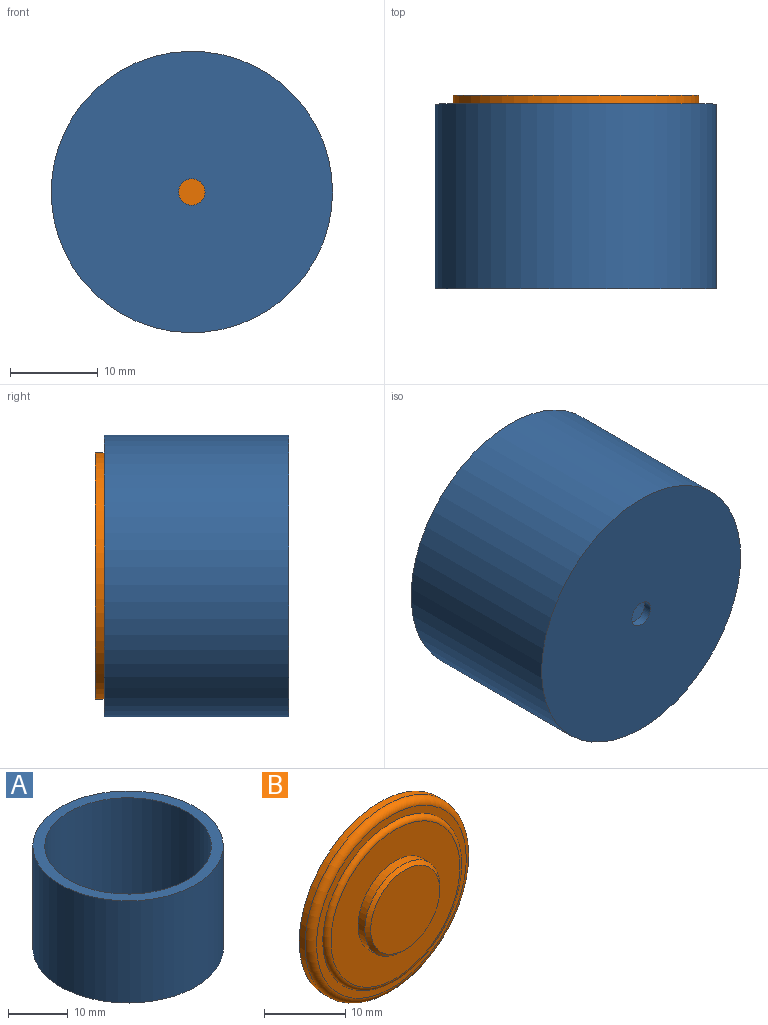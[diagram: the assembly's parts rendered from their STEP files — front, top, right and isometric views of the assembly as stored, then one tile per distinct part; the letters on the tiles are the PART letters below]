
ASSEMBLY  parts=2 mates=1
PART A: 6 faces, bbox 32x32x21 mm
  f0: cylinder r=16mm len=32mm, axis (0,0,-1), area 2111.2mm2, adj f3,f5
  f1: cylinder r=1.5mm len=3mm, axis (0,0,-1), area 9.4mm2, adj f2,f3
  f2: plane 28x28mm, normal (0,0,1), area 608.7mm2, adj f1,f4
  f3: plane 32x32mm, normal (0,0,-1), area 797.2mm2, adj f0,f1
  f4: cylinder r=14mm len=28mm, axis (0,0,-1), area 1759.3mm2, adj f2,f5
  f5: plane 32x32mm, normal (0,0,1), area 188.5mm2, adj f0,f4
PART B: 13 faces, bbox 30.3x4.4x30.3 mm
  f0: torus R=11.2mm, axis (0,-1,0), area 80.5mm2, adj f1,f8
  f1: plane 22.4x22.4mm, normal (0,-1,0), area 261.3mm2, adj f0,f10
  f2: cone r=12.4mm half-angle=45deg, axis (0,1,0), area 110.2mm2, adj f3,f12
  f3: plane 23.8x23.8mm, normal (0,1,0), area 312.1mm2, adj f2,f4
  f4: torus R=5.5mm, axis (0,1,0), area 60.6mm2, adj f3,f5
  f5: plane 11x11mm, normal (0,1,0), area 95mm2, adj f4
  f6: torus R=13mm, axis (0,-1,0), area 134.6mm2, adj f7,f8
  f7: cylinder r=14mm len=28mm, axis (0,1,0), area 88mm2, adj f6,f12
  f8: plane 26x26mm, normal (0,-1,0), area 86mm2, adj f0,f6
  f9: cone r=6.25mm half-angle=45deg, axis (0,1,0), area 27.8mm2, adj f10,f11
  f10: cylinder r=6.5mm len=13mm, axis (0,-1,0), area 49mm2, adj f1,f9
  f11: plane 12x12mm, normal (0,-1,0), area 113.1mm2, adj f9
  f12: plane 28x28mm, normal (0,1,0), area 93mm2, adj f2,f7
PLACE A rot(axis=(-1,0,0),90deg) t=(0,-20,0)mm
PLACE B at identity
MATE fastened A.f0 <-> B.f0  axis (0,1,0) through (0,1,0)mm
